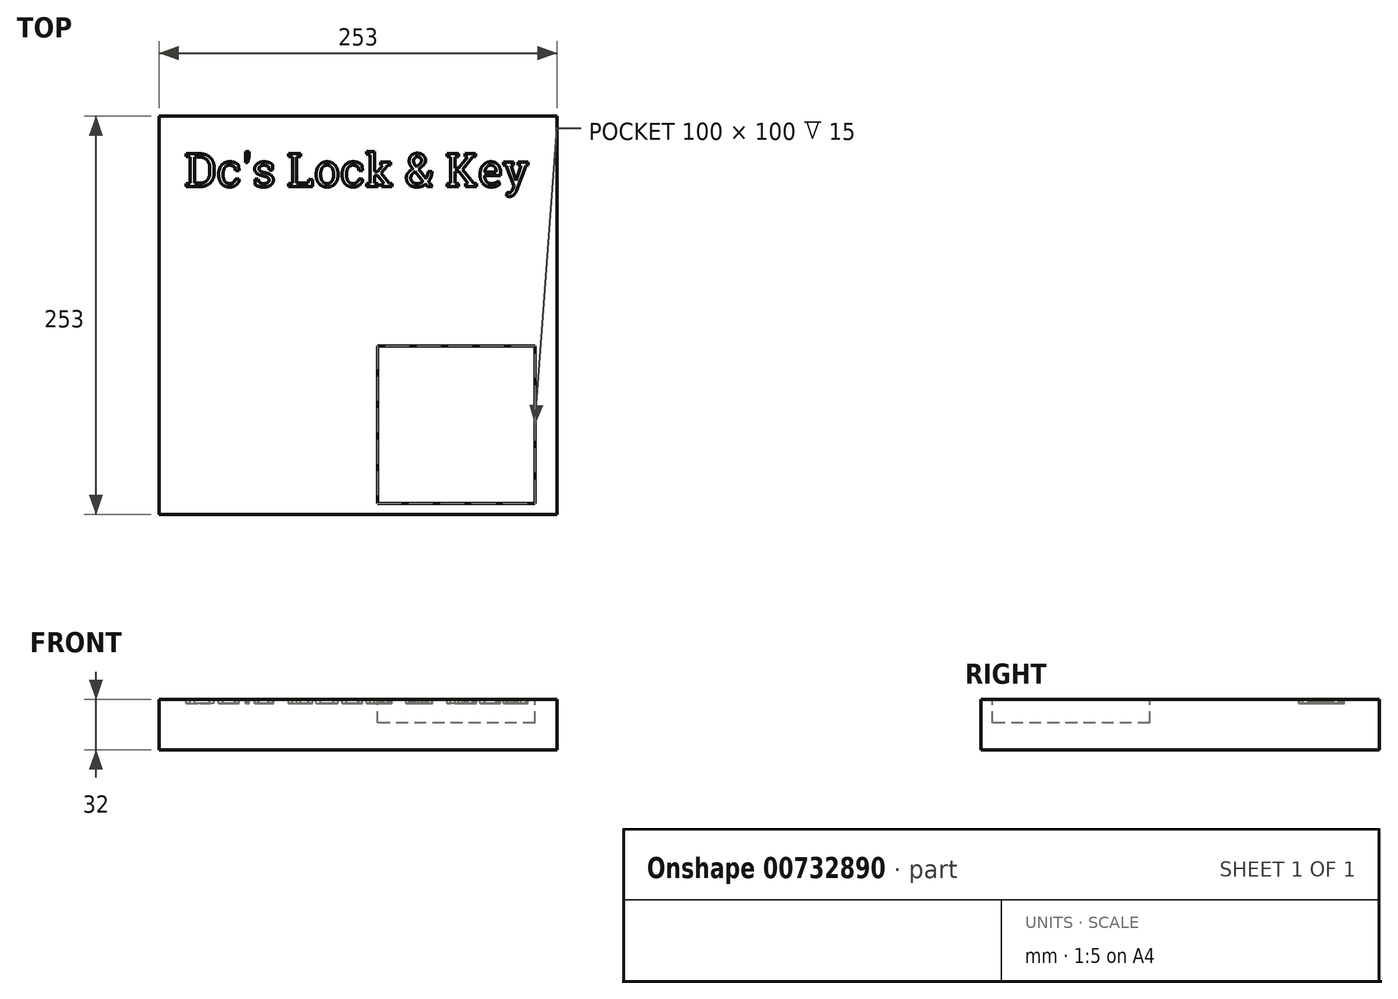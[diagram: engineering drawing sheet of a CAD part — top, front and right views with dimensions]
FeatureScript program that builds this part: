
annotation { "Feature Type Name" : "Feature", "Feature Type Description" : "" }
export const myFeature = defineFeature(function(context is Context, id is Id, definition is map)
    precondition{}
    {
        {
            var Q0;
            Q0=qCreatedBy(makeId("Top.planeOp"),FACE);
            var sketch = newSketch(context, id + "F0", { "sketchPlane" : qUnion([Q0])});
            skLineSegment(sketch, "E0.bottom", {"start": v(126.5, 126.5) * mm, "end": v(-126.5, 126.5) * mm});
            skLineSegment(sketch, "E0.top", {"start": v(126.5, -126.5) * mm, "end": v(-126.5, -126.5) * mm});
            skLineSegment(sketch, "E0.left", {"start": v(126.5, 126.5) * mm, "end": v(126.5, -126.5) * mm});
            skLineSegment(sketch, "E0.right", {"start": v(-126.5, 126.5) * mm, "end": v(-126.5, -126.5) * mm});
            skPoint(sketch, "E0.middle", {"position": v(0, 0) * mm});
            skSolve(sketch);
        }
        {
            var Q0;
            Q0=makeQuery(id+"F0.imprint","IMPRINT",FACE,{"disambiguationData":[TD([[makeQuery(id+"F0.imprint","IMPRINT",EDGE,{"derivedFrom":sQuery(id+"F0.wireOp",EDGE,"E0.bottom")}),1.0]])]});
            extrude(context, id + "F1", {"entities" : qUnion([Q0]), "depth" : 32 * mm, "offsetDistance" : 25 * mm});
        }
        {
            var Q0;
            Q0=makeQuery(id+"F1.opExtrude","CAP_FACE",FACE,{"disambiguationData":[OSD([sQuery(id+"F0.wireOp",EDGE,"E0.bottom"),sQuery(id+"F0.wireOp",EDGE,"E0.top"),sQuery(id+"F0.wireOp",EDGE,"E0.left"),sQuery(id+"F0.wireOp",EDGE,"E0.right")])],"isStart":false});
            var sketch = newSketch(context, id + "F2", { "sketchPlane" : qUnion([Q0])});
            skText(sketch, "E1", { "text": "Dc\'s Lock & Key", "fontName": "RobotoSlab-Regular.ttf"});
            const initialGuessF2  = {"E1": [-0.11017, 0.08172, 1, 0, 0.02115]};
            skSetInitialGuess(sketch, initialGuessF2);
            skSolve(sketch);
        }
        {
            var Q0;
            Q0 = qSketchRegion(id + "F2", true);
            extrude(context, id + "F3", {"entities" : qUnion([Q0]), "operationType" : NewBodyOperationType.REMOVE, "endBound" : BoundingType.SYMMETRIC, "oppositeDirection" : true, "depth" : 5 * mm, "offsetDistance" : 25 * mm});
        }
        {
            var Q0;
            {var subQ0=sQuery(id+"F0.wireOp",EDGE,"E0.left");var subQ1=sQuery(id+"F0.wireOp",EDGE,"E0.bottom");var subQ2=sQuery(id+"F0.wireOp",EDGE,"E0.right");var subQ3=sQuery(id+"F0.wireOp",EDGE,"E0.top");Q0=makeQuery(id+"F3.boolean.opBoolean","SPLIT",FACE,{"disambiguationData":[TD([makeQuery(id+"F1.opExtrude","SWEPT_FACE",FACE,{"disambiguationData":[OSD([subQ1])]})])],"derivedFrom":makeQuery(id+"F1.opExtrude","CAP_FACE",FACE,{"disambiguationData":[OSD([subQ1,subQ3,subQ0,subQ2])],"isStart":false})});}
            var sketch = newSketch(context, id + "F4", { "sketchPlane" : qUnion([Q0])});
            skLineSegment(sketch, "E2.bottom", {"start": v(112.26, -19.4) * mm, "end": v(12.26, -19.4) * mm});
            skLineSegment(sketch, "E2.top", {"start": v(112.26, -119.4) * mm, "end": v(12.26, -119.4) * mm});
            skLineSegment(sketch, "E2.left", {"start": v(112.26, -19.4) * mm, "end": v(112.26, -119.4) * mm});
            skLineSegment(sketch, "E2.right", {"start": v(12.26, -19.4) * mm, "end": v(12.26, -119.4) * mm});
            skPoint(sketch, "E2.middle", {"position": v(62.26, -69.4) * mm});
            skLineSegment(sketch, "E3.bottom", {"start": v(112.26, 0) * mm, "end": v(12.26, 0) * mm});
            skLineSegment(sketch, "E3.top", {"start": v(112.26, 100) * mm, "end": v(12.26, 100) * mm});
            skLineSegment(sketch, "E3.left", {"start": v(112.26, 0) * mm, "end": v(112.26, 100) * mm});
            skLineSegment(sketch, "E3.right", {"start": v(12.26, 0) * mm, "end": v(12.26, 100) * mm});
            skPoint(sketch, "E3.middle", {"position": v(62.26, 50) * mm});
            skSolve(sketch);
        }
        {
            var Q0;
            Q0=makeQuery(id+"F4.imprint","IMPRINT",FACE,{"disambiguationData":[TD([[makeQuery(id+"F4.imprint","IMPRINT",EDGE,{"derivedFrom":sQuery(id+"F4.wireOp",EDGE,"E2.bottom")}),1.0]])]});
            extrude(context, id + "F5", {"entities" : qUnion([Q0]), "operationType" : NewBodyOperationType.REMOVE, "oppositeDirection" : true, "depth" : 15 * mm, "offsetDistance" : 25 * mm});
        }
    });
